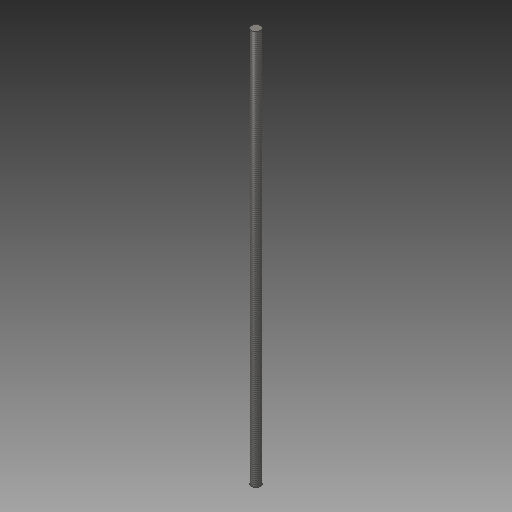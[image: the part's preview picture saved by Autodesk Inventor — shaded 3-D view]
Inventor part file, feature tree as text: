
AUTODESK INVENTOR PART (.ipt)
format: ipt  version: 2019 (Build 230136000, 136)  size: 86,528 bytes
history: native  units: mm
features: sketch x1, plane x1, extrude x1, thread x1
ambient origin geometry x8: Origin, YZ Plane, XZ Plane, XY Plane, X Axis, Y Axis, Z Axis, Center Point
bodies: Body1 (feature_tree)
feature tree (4):
  sketch  "Sketch1"  dims[d0=8.0mm d8=350.0mm d9=10.0mm d10=0.0mm d11=10.0mm d12=0.0mm]
  plane  "Work Plane4"
  extrude  "Extrusion2"  Depth=350.0mm
  thread  "Thread2"  [1 undecoded]
note: 1 required parameter value undecoded (feature->parameter linkage not recoverable at this tier; creation-order binding heuristic only, values carry confidence <= 0.55)
